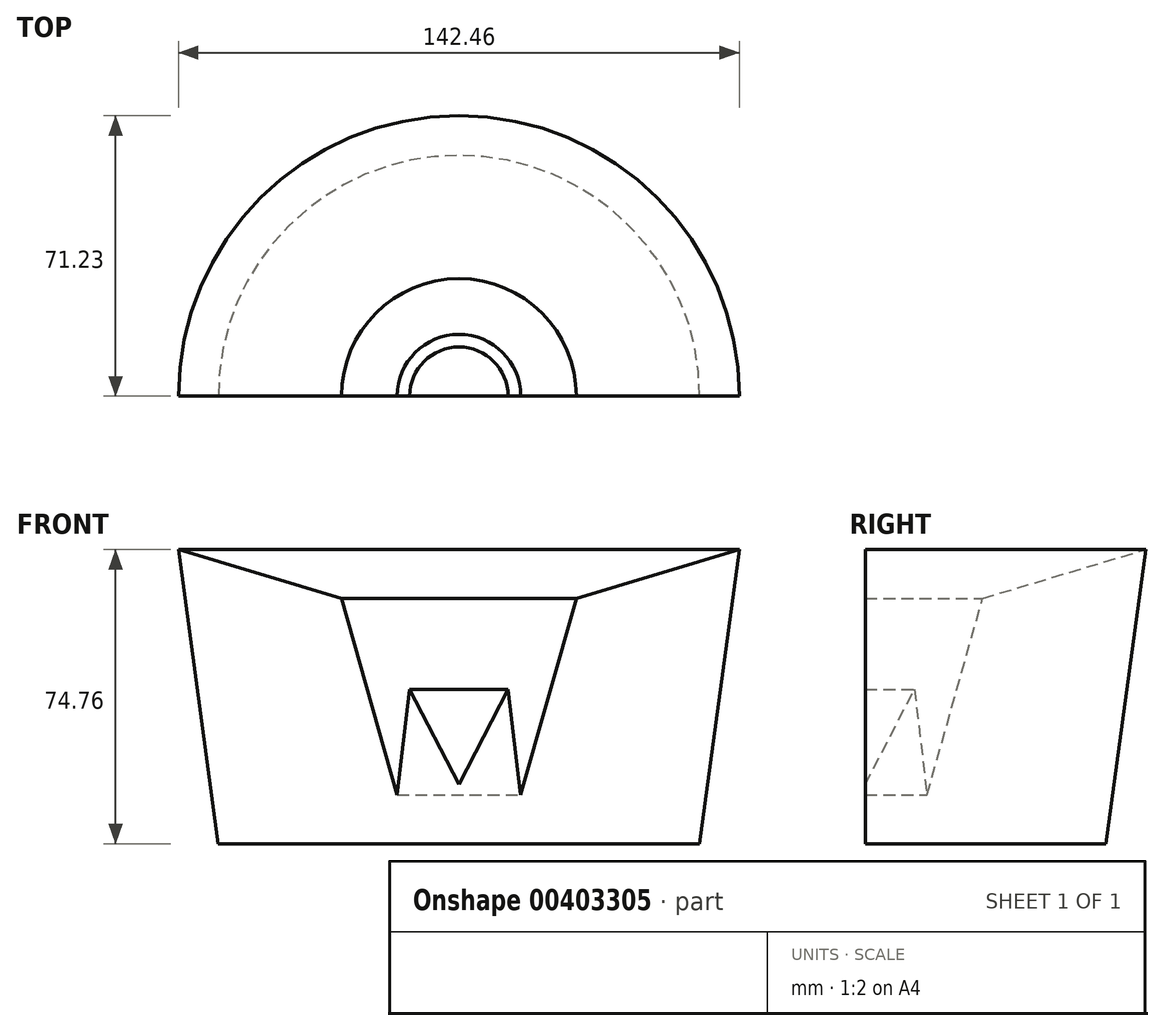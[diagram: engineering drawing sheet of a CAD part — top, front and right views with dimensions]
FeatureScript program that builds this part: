
annotation { "Feature Type Name" : "Feature", "Feature Type Description" : "" }
export const myFeature = defineFeature(function(context is Context, id is Id, definition is map)
    precondition{}
    {
        {
            var Q0;
            Q0=qCreatedBy(makeId("Front.planeOp"),FACE);
            var sketch = newSketch(context, id + "F0", { "sketchPlane" : qUnion([Q0])});
            skLineSegment(sketch, "E0", {"start": v(0, 15.08) * mm, "end": v(0, 0) * mm});
            skLineSegment(sketch, "E1", {"start": v(0, 0) * mm, "end": v(61.15, 0) * mm});
            skLineSegment(sketch, "E2", {"start": v(61.15, 0) * mm, "end": v(71.23, 74.76) * mm});
            skLineSegment(sketch, "E3", {"start": v(71.23, 74.76) * mm, "end": v(29.82, 62.35) * mm});
            skLineSegment(sketch, "E4", {"start": v(0, 15.08) * mm, "end": v(12.49, 39.25) * mm});
            skLineSegment(sketch, "E5", {"start": v(12.49, 39.25) * mm, "end": v(15.68, 12.41) * mm});
            skLineSegment(sketch, "E6", {"start": v(15.68, 12.41) * mm, "end": v(29.82, 62.35) * mm});
            skSolve(sketch);
        }
        {
            var Q0;
            Q0=makeQuery(id+"F0.imprint","IMPRINT",FACE,{"disambiguationData":[TD([[makeQuery(id+"F0.imprint","IMPRINT",EDGE,{"derivedFrom":sQuery(id+"F0.wireOp",EDGE,"E0")}),1.0]])]});
            var Q1;
            Q1=sQuery(id+"F0.wireOp",EDGE,"E0");
            revolve(context, id + "F1", {"entities" : qUnion([Q0]), "axis" : qUnion([Q1]), "revolveType" : RevolveType.ONE_DIRECTION, "oppositeDirection" : true, "angle" : 180 * degree});
        }
        {
            var Q0;
            Q0=qCreatedBy(makeId("Front.planeOp"),FACE);
            var sketch = newSketch(context, id + "F2", { "sketchPlane" : qUnion([Q0])});
            skCircle(sketch, "E7", {"center": v(42, -42.18) * mm, "radius": 15.88 * mm});
            skSolve(sketch);
        }
        {
            var Q0;
            Q0=sQuery(id+"F2.wireOp",EDGE,"E7");
            var Q1;
            Q1=sQuery(id+"F0.wireOp",EDGE,"E0");
            revolve(context, id + "F3", {"bodyType" : ToolBodyType.SURFACE, "surfaceEntities" : qUnion([Q0]), "axis" : qUnion([Q1]), "revolveType" : RevolveType.FULL});
        }
    });
